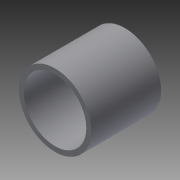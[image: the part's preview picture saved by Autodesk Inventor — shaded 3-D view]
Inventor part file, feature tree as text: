
AUTODESK INVENTOR PART (.ipt)
format: ipt  version: 2013 (Build 170138000, 138)  size: 79,872 bytes
history: native  units: in
note: dims shown in document units (in); Inventor stores cm internally (conversion verified against a paired STEP export)
features: extrude x1, sketch x1
ambient origin geometry x8: Origin, YZ Plane, XZ Plane, XY Plane, X Axis, Y Axis, Z Axis, Center Point
bodies: Solid1 (feature_tree)
feature tree (2):
  extrude  "Extrusion1"  Depth=1.25in
  sketch  "Sketch1"  dims[d0=1.45in d1=1.25in d2=1.4in d3=0.0in]
